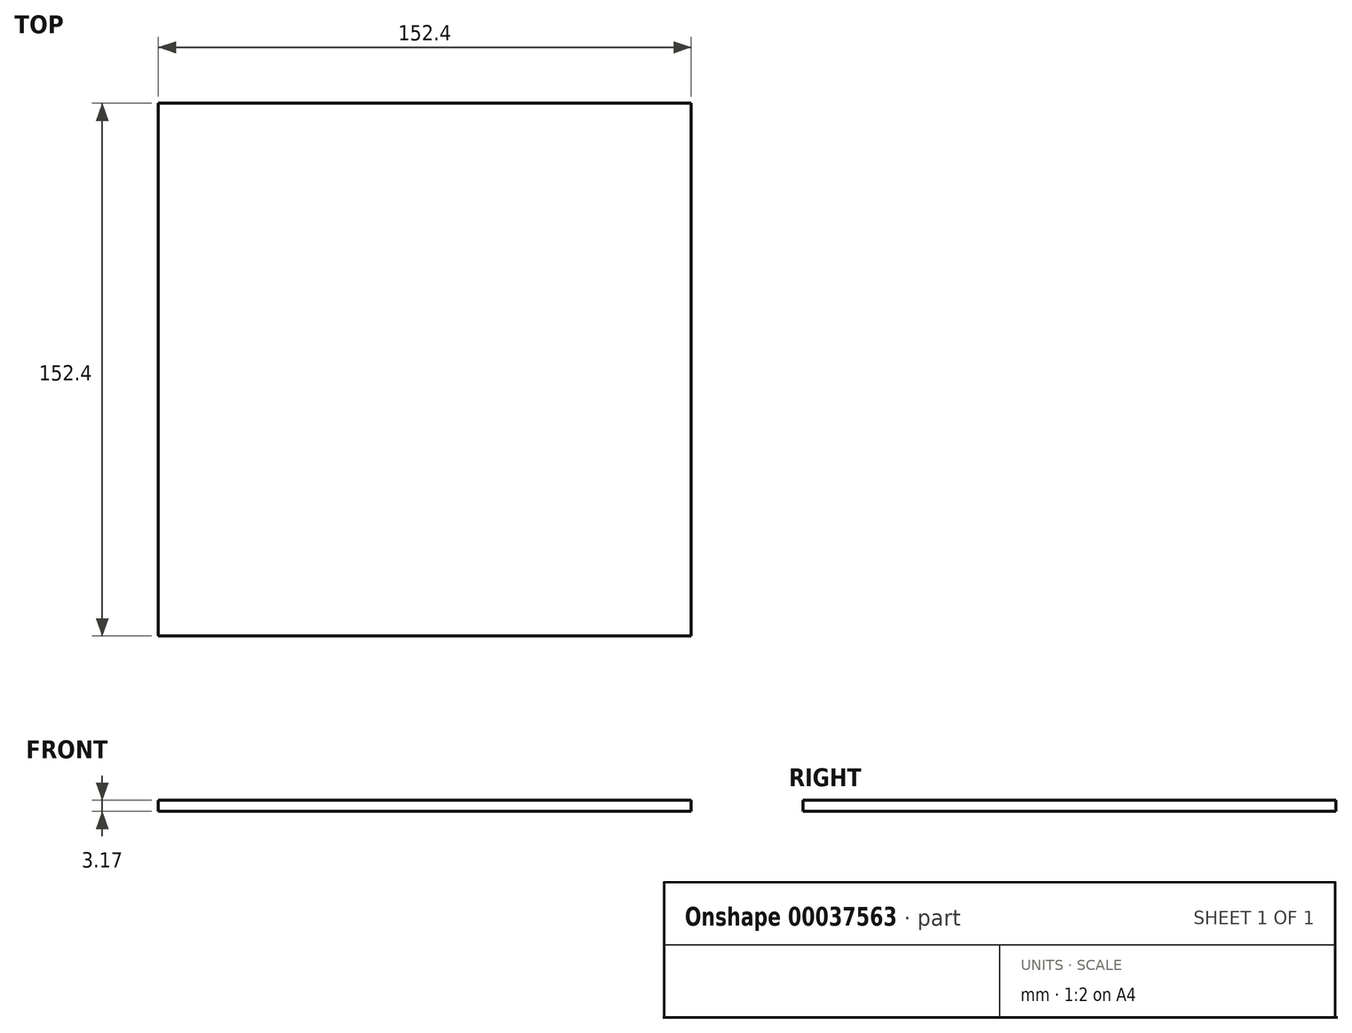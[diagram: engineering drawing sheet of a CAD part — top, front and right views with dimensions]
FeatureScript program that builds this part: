
annotation { "Feature Type Name" : "Feature", "Feature Type Description" : "" }
export const myFeature = defineFeature(function(context is Context, id is Id, definition is map)
    precondition{}
    {
        {
            var Q0;
            Q0=qCreatedBy(makeId("Top.planeOp"),FACE);
            var sketch = newSketch(context, id + "F0", { "sketchPlane" : qUnion([Q0])});
            skLineSegment(sketch, "E0.rect.bottom", {"start": v(76.2, -76.2) * mm, "end": v(-76.2, -76.2) * mm});
            skLineSegment(sketch, "E0.rect.top", {"start": v(76.2, 76.2) * mm, "end": v(-76.2, 76.2) * mm});
            skLineSegment(sketch, "E0.rect.left", {"start": v(76.2, -76.2) * mm, "end": v(76.2, 76.2) * mm});
            skLineSegment(sketch, "E0.rect.right", {"start": v(-76.2, -76.2) * mm, "end": v(-76.2, 76.2) * mm});
            skPoint(sketch, "E0.rect.middle", {"position": v(0, 0) * mm});
            skSolve(sketch);
        }
        {
            var Q0;
            Q0=makeQuery(id+"F0.imprint","IMPRINT",FACE,{"disambiguationData":[TD([[makeQuery(id+"F0.imprint","IMPRINT",EDGE,{"derivedFrom":sQuery(id+"F0.wireOp",EDGE,"E0.rect.bottom")}),-1.0]])]});
            extrude(context, id + "F1", {"entities" : qUnion([Q0]), "depth" : 3.17 * mm});
        }
    });
